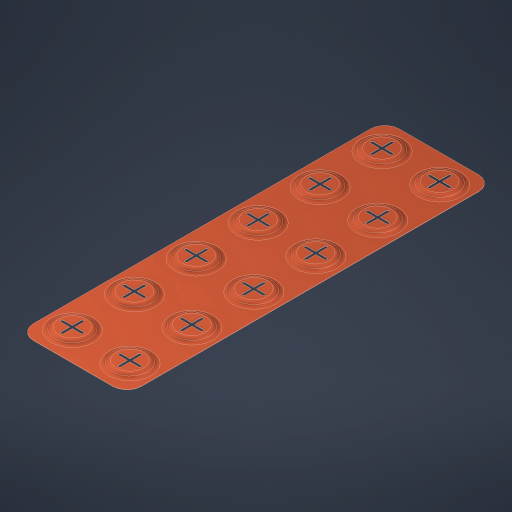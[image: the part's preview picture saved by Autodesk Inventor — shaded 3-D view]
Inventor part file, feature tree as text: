
AUTODESK INVENTOR PART (.ipt)
format: ipt  version: 2024.3 (Build 283343010, 343A)  size: 591,872 bytes
history: native  units: mm
features: sketch x2, extrude x2, fillet x1, pattern_linear x1, shell x1, other x1
ambient origin geometry x8: Origin, YZ Plane, XZ Plane, XY Plane, X Axis, Y Axis, Z Axis, Center Point
bodies: Volumenkörper1 (feature_tree)
feature tree (8):
  sketch  "Skizze1"  dims[d0=10.0mm d1=10.0mm]
  extrude  "Extrusion1"  Depth=10.0mm
  extrude  "Extrusion2"  Depth=0.5mm
  fillet  "Rundung1"  Radius=9.75mm
  pattern_linear  "Rechteckige Anordnung1"  Spacing1=8.75mm  [1 undecoded]
  shell  "Wandung1"  Thickness=8.75mm
  sketch  "Skizze2"  dims[d2=20.0mm d4=20.0mm d5=60.0mm d7=21.5mm d11=9.75mm d12=9.75mm d13=8.75mm d14=8.75mm d15=20.0mm d16=1.0mm d17=7.0mm d18=8.75mm d19=20.0mm d21=20.0mm d22=60.0mm d24=21.5mm d27=5.0mm d28=8.75mm d29=10.0mm d30=0.0mm d32=13.0mm d33=1.0mm d34=0.0mm d35=2.0mm d36=20.0mm d38=20.0mm d39=60.0mm d41=21.5mm d42=0.15mm d43=0.5mm d44=0.5mm d45=0.0mm]
  other  "Ausschneiden1"
note: 1 required parameter value undecoded (feature->parameter linkage not recoverable at this tier; creation-order binding heuristic only, values carry confidence <= 0.55)
